# Revit family: HARMANN - REVIT- MOVO.S
name_source: partatom
category: Wyposażenie mechaniczne
units: mm (PartAtom-declared; Revit-internal decimal feet)

## family parameters
Numer OmniClass = 23.75.00.00
Oparty na płaszczyźnie roboczej = Nie
Punkt obliczania pomieszczeń = Nie
Tnij formami wycięć po wczytaniu = Nie
Typ części = Normalny
Tytuł OmniClass = Climate Control (HVAC)
Współdzielony = Nie
Wymiar okrągłego złącza = Użyj średnicy
Zachowaj orientację opisów = Nie
Zawsze pionowo = Tak

## types (13) — shared parameters
Autor = https://www.archispace.com
Lookup Table Name = MOVO
Opc Brak podstawy = Podstawa : Brak podstawy
Opc Podstawa Dachowa PR = Podstawa : Podstawa PR
Opis = Dachowy wentylator z wyrzutem pionowym
Podstawa A = Podstawa : Brak podstawy
Podstawa B = Podstawa : Podstawa PR
Producent = Harmann Polska Sp. z o.o.
Zasilanie Częstotliwość Maksymalna fmax = 50 Hz
Zasilanie Częstotliwość Nominalna fnom = 50 Hz
Zasilanie Ilość faz = 3
Zasilanie napięcie nominalne Unom = 400 V
zero-valued in all types: Domyślna rzędna

## per-type parameters (varying)
| type | Akc D | Akc EP | Akc PR | Akc SL | Ciśnienie akustyczne nominalne obudowa Lpa | DN | MOVO S | Masa | Model | N1 | Numer artykułu | Obroty nominalne nnom | Powietrze Przepływ Maksymalny Qmax | Powietrze ciśnienie statyczne maksymalne dPmax | Temperatura pracy ciągłej maksymalna T | Zasilanie Częstotliwość Minimalna fmin | Zasilanie Moc maksymalna Pmax | Zasilanie natężenie maksymalne Imax |
| MOVO.S 6-800/26000T | HARMANN - Akcesoria - D : D 710s | HARMANN - Akcesoria - EP : EP 710 | HARMANN - Akcesoria - PR : PR 800/710 | HARMANN - Akcesoria - SL : SL 710 | 73 dB(A) | 710 mm | HARMANN - Akcesoria - MOVO_S : MOVO.S 6-800/26000T | 340.00 kg | MOVO.S 6-800/26000T | 12 mm | 2250011 | 970.000 obr./min | 26000.00 m³/h | 820.0 Pa | 50 °C | 25 Hz | 5500 W | 12 A |
| MOVO.S 4-800/39500T | HARMANN - Akcesoria - D : D 710s | HARMANN - Akcesoria - EP : EP 710 | HARMANN - Akcesoria - PR : PR 710/630 | HARMANN - Akcesoria - SL : SL 710 | 82 dB(A) | 710 mm | HARMANN - Akcesoria - MOVO_S : MOVO.S 4-800/39500T | 390.00 kg | MOVO.S 4-800/39500T | 11 mm | 2250010 | 1460.000 obr./min | 39500.00 m³/h | 1980.0 Pa | 50 °C | 25 Hz | 15000 W | 28 A |
| MOVO.S 6-710/18300T | HARMANN - Akcesoria - D : D 630s | HARMANN - Akcesoria - EP : EP 630 | HARMANN - Akcesoria - PR : PR 710/630 | HARMANN - Akcesoria - SL : SL 630 | 70 dB(A) | 630 mm  [stored 2.06693 ft] | HARMANN - Akcesoria - MOVO_S : MOVO.S 6-710/18300T | 240.00 kg | MOVO.S 6-710/18300T | 10 mm | 2250007 | 970.000 obr./min | 18300.00 m³/h | 680.0 Pa | 50 °C | 25 Hz | 3000 W | 7 A |
| MOVO.S 4-710/27500T | HARMANN - Akcesoria - D : D 630s | HARMANN - Akcesoria - EP : EP 630 | HARMANN - Akcesoria - PR : PR 710/630 | HARMANN - Akcesoria - SL : SL 630 | 79 dB(A) | 630 mm  [stored 2.06693 ft] | HARMANN - Akcesoria - MOVO_S : MOVO.S 4-710/27500T | 250.00 kg | MOVO.S 4-710/27500T | 9 mm | 2250006 | 1450.000 obr./min | 27500.00 m³/h | 1550.0 Pa | 50 °C | 25 Hz | 11000 W | 21 A |
| MOVO.S 4-710/23700T | HARMANN - Akcesoria - D : D 630s | HARMANN - Akcesoria - EP : EP 630 | HARMANN - Akcesoria - PR : PR 710/630 | HARMANN - Akcesoria - SL : SL 630 | 78 dB(A) | 630 mm  [stored 2.06693 ft] | HARMANN - Akcesoria - MOVO_S : MOVO.S 4-710/23700T | 250.00 kg | MOVO.S 4-710/23700T | 9 mm | 2250005 | 1450.000 obr./min | 23700.00 m³/h | 1300.0 Pa | 50 °C | 25 Hz | 7500 W | 14 A |
| MOVO.S 6-630/12900T | HARMANN - Akcesoria - D : D 560s | HARMANN - Akcesoria - EP : EP 560 | HARMANN - Akcesoria - PR : PR 630/560 | HARMANN - Akcesoria - SL : SL 560 | 66 dB | 560 mm  [stored 1.83727 ft] | HARMANN - Akcesoria - MOVO_S : MOVO.S 6-630/12900T | 130.00 kg | MOVO.S 6-630/12900T | 8 mm | 2250002 | 940.000 obr./min | 12900.00 m³/h | 550.0 Pa | 50 °C | 25 Hz | 2200 W | 5 A |
| MOVO.S 4-630/19300T | HARMANN - Akcesoria - D : D 560s | HARMANN - Akcesoria - EP : EP 560 | HARMANN - Akcesoria - PR : PR 630/560 | HARMANN - Akcesoria - SL : SL 560 | 75 dB(A) | 560 mm  [stored 1.83727 ft] | HARMANN - Akcesoria - MOVO_S : MOVO.S 4-630/19300T | 130.00 kg | MOVO.S 4-630/19300T | 7 mm | 2250001 | 1455.000 obr./min | 19300.00 m³/h | 1200.0 Pa | 50 °C | 25 Hz | 5500 W | 11 A |
| MOVO.S 6-900/37000T | HARMANN - Akcesoria - D : D 800s | HARMANN - Akcesoria - EP : EP 800 | HARMANN - Akcesoria - PR : PR 900/800 | HARMANN - Akcesoria - SL : SL 800 | 77 dB(A) | 800 mm  [stored 2.62467 ft] | HARMANN - Akcesoria - MOVO_S : MOVO.S 6-900/37000T | 410.00 kg | MOVO.S 6-800/37000T | 12 mm | 2250014 | 965.000 obr./min | 37000.00 m³/h | 1050.0 Pa | 50 °C | 25 Hz | 7500 W | 16 A |
| MOVO.S 6-1000/43100T | HARMANN - Akcesoria - D : D 900s | HARMANN - Akcesoria - EP : EP 900 | HARMANN - Akcesoria - PR : PR 1000/900 | HARMANN - Akcesoria - SL : SL 900 | 73 dB(A) | 900 mm  [stored 2.95276 ft] | HARMANN - Akcesoria - MOVO_S : MOVO.S 6-1000/52000T | 370.00 kg | MOVO.S 6-800/22900T EX | 12 mm | 78252004 | 1440.000 obr./min | 22900.00 m³/h | 810.0 Pa | 40 °C | 30 Hz | 5500 W | 12 A |
| MOVO.S 6-1000/52000T | HARMANN - Akcesoria - D : D 900s | HARMANN - Akcesoria - EP : EP 900 | HARMANN - Akcesoria - PR : PR 1000/900 | HARMANN - Akcesoria - SL : SL 900 | 73 dB(A) | 900 mm  [stored 2.95276 ft] | HARMANN - Akcesoria - MOVO_S : MOVO.S 6-1000/52000T | 370.00 kg | MOVO.S 6-800/22900T EX | 12 mm | 78252004 | 1440.000 obr./min | 22900.00 m³/h | 810.0 Pa | 40 °C | 30 Hz | 5500 W | 12 A |
| MOVO.S 8-1000/38000T | HARMANN - Akcesoria - D : D 900s | HARMANN - Akcesoria - EP : EP 900 | HARMANN - Akcesoria - PR : PR 1000/900 | HARMANN - Akcesoria - SL : SL 900 | 73 dB(A) | 900 mm  [stored 2.95276 ft] | HARMANN - Akcesoria - MOVO_S : MOVO.S 6-1000/52000T | 370.00 kg | MOVO.S 6-800/22900T EX | 12 mm | 78252004 | 1440.000 obr./min | 22900.00 m³/h | 810.0 Pa | 40 °C | 30 Hz | 5500 W | 12 A |
| MOVO.S 8-1000/32000T | HARMANN - Akcesoria - D : D 900s | HARMANN - Akcesoria - EP : EP 900 | HARMANN - Akcesoria - PR : PR 1000/900 | HARMANN - Akcesoria - SL : SL 900 | 73 dB(A) | 900 mm  [stored 2.95276 ft] | HARMANN - Akcesoria - MOVO_S : MOVO.S 6-1000/52000T | 370.00 kg | MOVO.S 6-800/22900T EX | 12 mm | 78252004 | 1440.000 obr./min | 22900.00 m³/h | 810.0 Pa | 40 °C | 30 Hz | 5500 W | 12 A |
| MOVO.S 8-900/27500T | HARMANN - Akcesoria - D : D 800s | HARMANN - Akcesoria - EP : EP 800 | HARMANN - Akcesoria - PR : PR 900/800 | HARMANN - Akcesoria - SL : SL 800 | 77 dB(A) | 800 mm  [stored 2.62467 ft] | HARMANN - Akcesoria - MOVO_S : MOVO.S 6-900/37000T | 410.00 kg | MOVO.S 6-800/37000T | 12 mm | 2250014 | 965.000 obr./min | 37000.00 m³/h | 1050.0 Pa | 50 °C | 25 Hz | 7500 W | 16 A |

note: [stored X ft] marks values corroborated as IEEE doubles in the binary element streams (Revit-internal decimal feet)

## geometry (parser evidence)
native form markers: Sweep x18
no freeform markers — native parametric forms only
